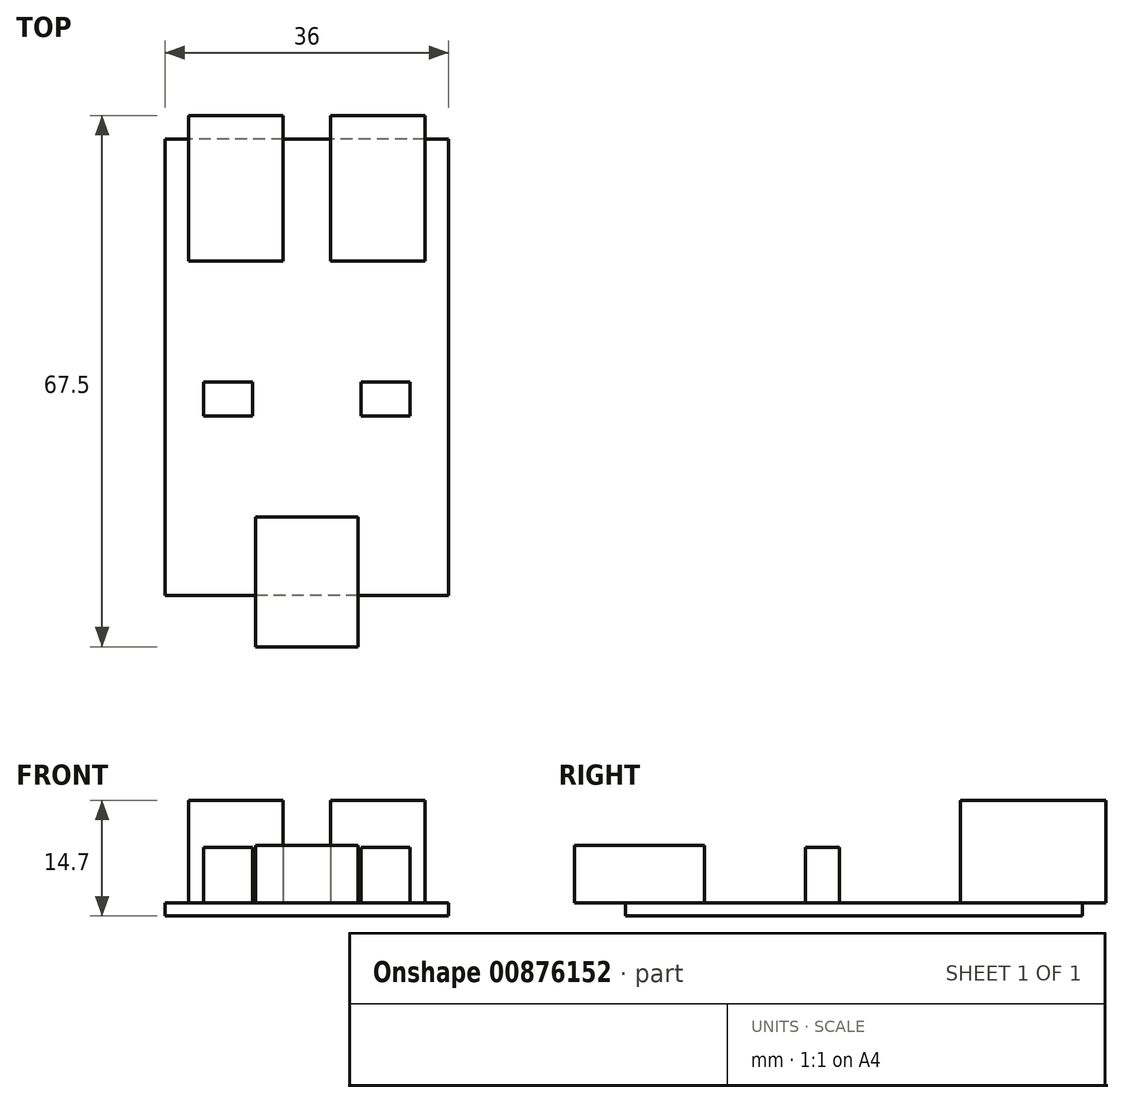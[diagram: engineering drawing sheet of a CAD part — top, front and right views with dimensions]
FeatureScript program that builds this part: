
annotation { "Feature Type Name" : "Feature", "Feature Type Description" : "" }
export const myFeature = defineFeature(function(context is Context, id is Id, definition is map)
    precondition{}
    {
        {
            var Q0;
            Q0=qCreatedBy(makeId("Top.planeOp"),FACE);
            var sketch = newSketch(context, id + "F0", { "sketchPlane" : qUnion([Q0])});
            skLineSegment(sketch, "E0.bottom", {"start": v(18, 29) * mm, "end": v(-18, 29) * mm});
            skLineSegment(sketch, "E0.top", {"start": v(18, -29) * mm, "end": v(-18, -29) * mm});
            skLineSegment(sketch, "E0.left", {"start": v(18, 29) * mm, "end": v(18, -29) * mm});
            skLineSegment(sketch, "E0.right", {"start": v(-18, 29) * mm, "end": v(-18, -29) * mm});
            skPoint(sketch, "E0.middle", {"position": v(0, 0) * mm});
            skLineSegment(sketch, "E1.bottom", {"start": v(-15, 13.5) * mm, "end": v(-3, 13.5) * mm});
            skLineSegment(sketch, "E1.top", {"start": v(-15, 32) * mm, "end": v(-3, 32) * mm});
            skLineSegment(sketch, "E1.left", {"start": v(-15, 13.5) * mm, "end": v(-15, 32) * mm});
            skLineSegment(sketch, "E1.right", {"start": v(-3, 13.5) * mm, "end": v(-3, 32) * mm});
            skLineSegment(sketch, "E2.bottom", {"start": v(3, 13.5) * mm, "end": v(15, 13.5) * mm});
            skLineSegment(sketch, "E2.top", {"start": v(3, 32) * mm, "end": v(15, 32) * mm});
            skLineSegment(sketch, "E2.left", {"start": v(3, 13.5) * mm, "end": v(3, 32) * mm});
            skLineSegment(sketch, "E2.right", {"start": v(15, 13.5) * mm, "end": v(15, 32) * mm});
            skLineSegment(sketch, "E3.bottom", {"start": v(6.5, -19) * mm, "end": v(-6.5, -19) * mm});
            skLineSegment(sketch, "E3.top", {"start": v(6.5, -35.5) * mm, "end": v(-6.5, -35.5) * mm});
            skLineSegment(sketch, "E3.left", {"start": v(6.5, -19) * mm, "end": v(6.5, -35.5) * mm});
            skLineSegment(sketch, "E3.right", {"start": v(-6.5, -19) * mm, "end": v(-6.5, -35.5) * mm});
            skPoint(sketch, "E3.middle", {"position": v(0, -27.25) * mm});
            skLineSegment(sketch, "E4.bottom", {"start": v(6.9, -1.85) * mm, "end": v(13.1, -1.85) * mm});
            skLineSegment(sketch, "E4.top", {"start": v(6.9, -6.15) * mm, "end": v(13.1, -6.15) * mm});
            skLineSegment(sketch, "E4.left", {"start": v(6.9, -1.85) * mm, "end": v(6.9, -6.15) * mm});
            skLineSegment(sketch, "E4.right", {"start": v(13.1, -1.85) * mm, "end": v(13.1, -6.15) * mm});
            skPoint(sketch, "E4.middle", {"position": v(10, -4) * mm});
            skLineSegment(sketch, "E5.bottom", {"start": v(-13.1, -1.85) * mm, "end": v(-6.9, -1.85) * mm});
            skLineSegment(sketch, "E5.top", {"start": v(-13.1, -6.15) * mm, "end": v(-6.9, -6.15) * mm});
            skLineSegment(sketch, "E5.left", {"start": v(-13.1, -1.85) * mm, "end": v(-13.1, -6.15) * mm});
            skLineSegment(sketch, "E5.right", {"start": v(-6.9, -1.85) * mm, "end": v(-6.9, -6.15) * mm});
            skPoint(sketch, "E5.middle", {"position": v(-10, -4) * mm});
            skSolve(sketch);
        }
        {
            var Q0;
            {var subQ7=sQuery(id+"F0.wireOp",EDGE,"E0.left");Q0=makeQuery(id+"F0.imprint","IMPRINT",FACE,{"disambiguationData":[TD([[makeQuery(id+"F0.imprint","IMPRINT",EDGE,{"derivedFrom":subQ7}),-1.0]])]});}
            var Q1;
            {var subQ5=sQuery(id+"F0.wireOp",EDGE,"E2.bottom");Q1=makeQuery(id+"F0.imprint","IMPRINT",FACE,{"disambiguationData":[TD([[makeQuery(id+"F0.imprint","IMPRINT",EDGE,{"derivedFrom":subQ5}),1.0]])]});}
            var Q2;
            {var subQ5=sQuery(id+"F0.wireOp",EDGE,"E1.bottom");Q2=makeQuery(id+"F0.imprint","IMPRINT",FACE,{"disambiguationData":[TD([[makeQuery(id+"F0.imprint","IMPRINT",EDGE,{"derivedFrom":subQ5}),1.0]])]});}
            var Q3;
            {var subQ5=sQuery(id+"F0.wireOp",EDGE,"E3.bottom");Q3=makeQuery(id+"F0.imprint","IMPRINT",FACE,{"disambiguationData":[TD([[makeQuery(id+"F0.imprint","IMPRINT",EDGE,{"derivedFrom":subQ5}),1.0]])]});}
            var Q4;
            Q4=makeQuery(id+"F0.imprint","IMPRINT",FACE,{"disambiguationData":[TD([[makeQuery(id+"F0.imprint","IMPRINT",EDGE,{"derivedFrom":sQuery(id+"F0.wireOp",EDGE,"E4.bottom")}),-1.0]])]});
            var Q5;
            Q5=makeQuery(id+"F0.imprint","IMPRINT",FACE,{"disambiguationData":[TD([[makeQuery(id+"F0.imprint","IMPRINT",EDGE,{"derivedFrom":sQuery(id+"F0.wireOp",EDGE,"E5.bottom")}),-1.0]])]});
            extrude(context, id + "F1", {"entities" : qUnion([Q0, Q1, Q2, Q3, Q4, Q5]), "oppositeDirection" : true, "depth" : 1.7 * mm, "offsetDistance" : 25.4 * mm});
        }
        {
            var Q0;
            {var subQ5=sQuery(id+"F0.wireOp",EDGE,"E3.top");Q0=makeQuery(id+"F0.imprint","IMPRINT",FACE,{"disambiguationData":[TD([[makeQuery(id+"F0.imprint","IMPRINT",EDGE,{"derivedFrom":subQ5}),-1.0]])]});}
            var Q1;
            {var subQ5=sQuery(id+"F0.wireOp",EDGE,"E3.bottom");Q1=makeQuery(id+"F0.imprint","IMPRINT",FACE,{"disambiguationData":[TD([[makeQuery(id+"F0.imprint","IMPRINT",EDGE,{"derivedFrom":subQ5}),1.0]])]});}
            extrude(context, id + "F2", {"entities" : qUnion([Q0, Q1]), "depth" : 7.3 * mm, "offsetDistance" : 25.4 * mm});
        }
        {
            var Q0;
            {var subQ5=sQuery(id+"F0.wireOp",EDGE,"E1.top");Q0=makeQuery(id+"F0.imprint","IMPRINT",FACE,{"disambiguationData":[TD([[makeQuery(id+"F0.imprint","IMPRINT",EDGE,{"derivedFrom":subQ5}),-1.0]])]});}
            var Q1;
            {var subQ5=sQuery(id+"F0.wireOp",EDGE,"E1.bottom");Q1=makeQuery(id+"F0.imprint","IMPRINT",FACE,{"disambiguationData":[TD([[makeQuery(id+"F0.imprint","IMPRINT",EDGE,{"derivedFrom":subQ5}),1.0]])]});}
            var Q2;
            {var subQ5=sQuery(id+"F0.wireOp",EDGE,"E2.bottom");Q2=makeQuery(id+"F0.imprint","IMPRINT",FACE,{"disambiguationData":[TD([[makeQuery(id+"F0.imprint","IMPRINT",EDGE,{"derivedFrom":subQ5}),1.0]])]});}
            var Q3;
            {var subQ5=sQuery(id+"F0.wireOp",EDGE,"E2.top");Q3=makeQuery(id+"F0.imprint","IMPRINT",FACE,{"disambiguationData":[TD([[makeQuery(id+"F0.imprint","IMPRINT",EDGE,{"derivedFrom":subQ5}),-1.0]])]});}
            extrude(context, id + "F3", {"entities" : qUnion([Q0, Q1, Q2, Q3]), "operationType" : NewBodyOperationType.ADD, "depth" : 13 * mm, "offsetDistance" : 25.4 * mm});
        }
        {
            var Q0;
            Q0=makeQuery(id+"F0.imprint","IMPRINT",FACE,{"disambiguationData":[TD([[makeQuery(id+"F0.imprint","IMPRINT",EDGE,{"derivedFrom":sQuery(id+"F0.wireOp",EDGE,"E4.bottom")}),-1.0]])]});
            var Q1;
            Q1=makeQuery(id+"F0.imprint","IMPRINT",FACE,{"disambiguationData":[TD([[makeQuery(id+"F0.imprint","IMPRINT",EDGE,{"derivedFrom":sQuery(id+"F0.wireOp",EDGE,"E5.bottom")}),-1.0]])]});
            extrude(context, id + "F4", {"entities" : qUnion([Q0, Q1]), "depth" : 7 * mm, "offsetDistance" : 25.4 * mm});
        }
    });
